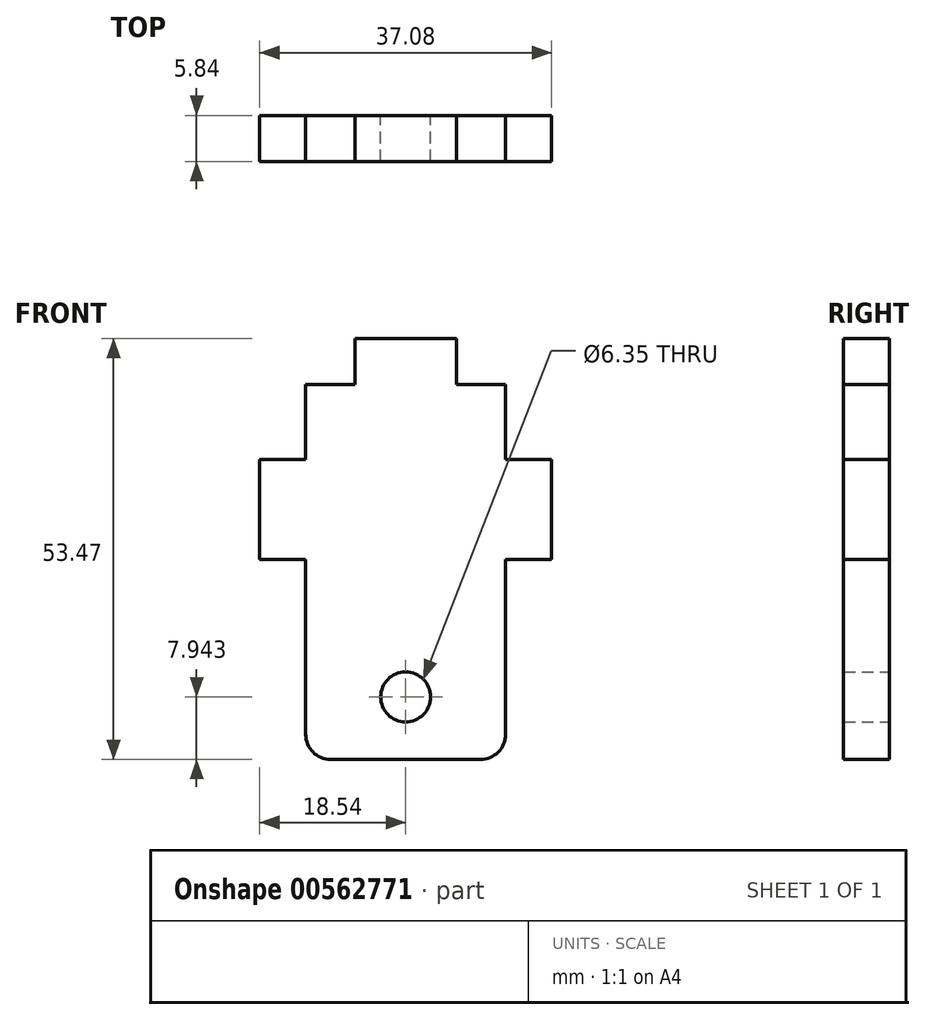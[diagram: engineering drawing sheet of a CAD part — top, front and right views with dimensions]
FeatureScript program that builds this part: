
annotation { "Feature Type Name" : "Feature", "Feature Type Description" : "" }
export const myFeature = defineFeature(function(context is Context, id is Id, definition is map)
    precondition{}
    {
        {
            var Q0;
            Q0=qCreatedBy(makeId("Front.planeOp"),FACE);
            var sketch = newSketch(context, id + "F0", { "sketchPlane" : qUnion([Q0])});
            skLineSegment(sketch, "E0.left", {"start": v(-12.7, 25.4) * mm, "end": v(-12.7, 15.88) * mm});
            skLineSegment(sketch, "E1", {"start": v(-12.7, 9.53) * mm, "end": v(12.7, 9.53) * mm, "construction": true});
            skLineSegment(sketch, "E2", {"start": v(0, 25.4) * mm, "end": v(0, -6.35) * mm, "construction": true});
            skLineSegment(sketch, "E3.top", {"start": v(-6.45, 31.24) * mm, "end": v(6.45, 31.24) * mm});
            skLineSegment(sketch, "E3.left", {"start": v(-6.45, 25.4) * mm, "end": v(-6.45, 31.24) * mm});
            skLineSegment(sketch, "E3.right", {"start": v(6.45, 25.4) * mm, "end": v(6.45, 31.24) * mm});
            skPoint(sketch, "E3.middle", {"position": v(0, 28.32) * mm});
            skLineSegment(sketch, "E4.trimOffspring", {"start": v(6.45, 25.4) * mm, "end": v(12.7, 25.4) * mm});
            skLineSegment(sketch, "E5", {"start": v(-12.7, 25.4) * mm, "end": v(-6.45, 25.4) * mm});
            skLineSegment(sketch, "E6.bottom", {"start": v(12.7, 15.88) * mm, "end": v(18.54, 15.88) * mm});
            skLineSegment(sketch, "E6.top", {"start": v(12.7, 3.18) * mm, "end": v(18.54, 3.18) * mm});
            skLineSegment(sketch, "E6.right", {"start": v(18.54, 15.88) * mm, "end": v(18.54, 3.18) * mm});
            skPoint(sketch, "E6.middle", {"position": v(15.62, 9.53) * mm});
            skLineSegment(sketch, "E7.trimOffspring", {"start": v(12.7, 3.18) * mm, "end": v(12.7, -6.35) * mm});
            skLineSegment(sketch, "E8", {"start": v(12.7, 15.88) * mm, "end": v(12.7, 25.4) * mm});
            skLineSegment(sketch, "E9.MirrorCS", {"start": v(-12.7, 3.18) * mm, "end": v(-12.7, -6.35) * mm});
            skLineSegment(sketch, "E10.MirrorCS", {"start": v(-12.7, 15.88) * mm, "end": v(-12.7, 25.4) * mm});
            skPoint(sketch, "E11.MirrorP", {"position": v(-15.62, 9.53) * mm});
            skLineSegment(sketch, "E12.MirrorCS", {"start": v(-12.7, 15.88) * mm, "end": v(-18.54, 15.88) * mm});
            skLineSegment(sketch, "E13.MirrorCS", {"start": v(-12.7, 3.18) * mm, "end": v(-18.54, 3.18) * mm});
            skLineSegment(sketch, "E14.MirrorCS", {"start": v(-18.54, 15.88) * mm, "end": v(-18.54, 3.18) * mm});
            skPoint(sketch, "E15.center.orphan", {"position": v(0, 0) * mm});
            skCircle(sketch, "E16", {"center": v(0, -14.29) * mm, "radius": 3.18 * mm});
            skLineSegment(sketch, "E17.top", {"start": v(-12.7, -22.22) * mm, "end": v(12.7, -22.22) * mm});
            skLineSegment(sketch, "E17.left", {"start": v(-12.7, -6.35) * mm, "end": v(-12.7, -22.22) * mm});
            skLineSegment(sketch, "E17.right", {"start": v(12.7, -6.35) * mm, "end": v(12.7, -22.22) * mm});
            skSolve(sketch);
        }
        {
            var Q0;
            Q0=qSketchRegion(id+"F0",true);
            extrude(context, id + "F1", {"entities" : qUnion([Q0]), "depth" : 5.84 * mm, "offsetDistance" : 25.4 * mm});
        }
        {
            var Q0;
            Q0=makeQuery(id+"F1.opExtrude","SWEPT_EDGE",EDGE,{"disambiguationData":[OSD([sQuery(id+"F0.wireOp",EDGE,"E17.top"),sQuery(id+"F0.wireOp",EDGE,"E17.left")])]});
            var Q1;
            Q1=makeQuery(id+"F1.opExtrude","SWEPT_EDGE",EDGE,{"disambiguationData":[OSD([sQuery(id+"F0.wireOp",EDGE,"E17.top"),sQuery(id+"F0.wireOp",EDGE,"E17.right")])]});
            fillet(context, id + "F2", {"entities" : qUnion([Q0, Q1]), "radius" : 3.17 * mm, "tangentPropagation" : true, "allowEdgeOverflow" : false});
        }
    });
